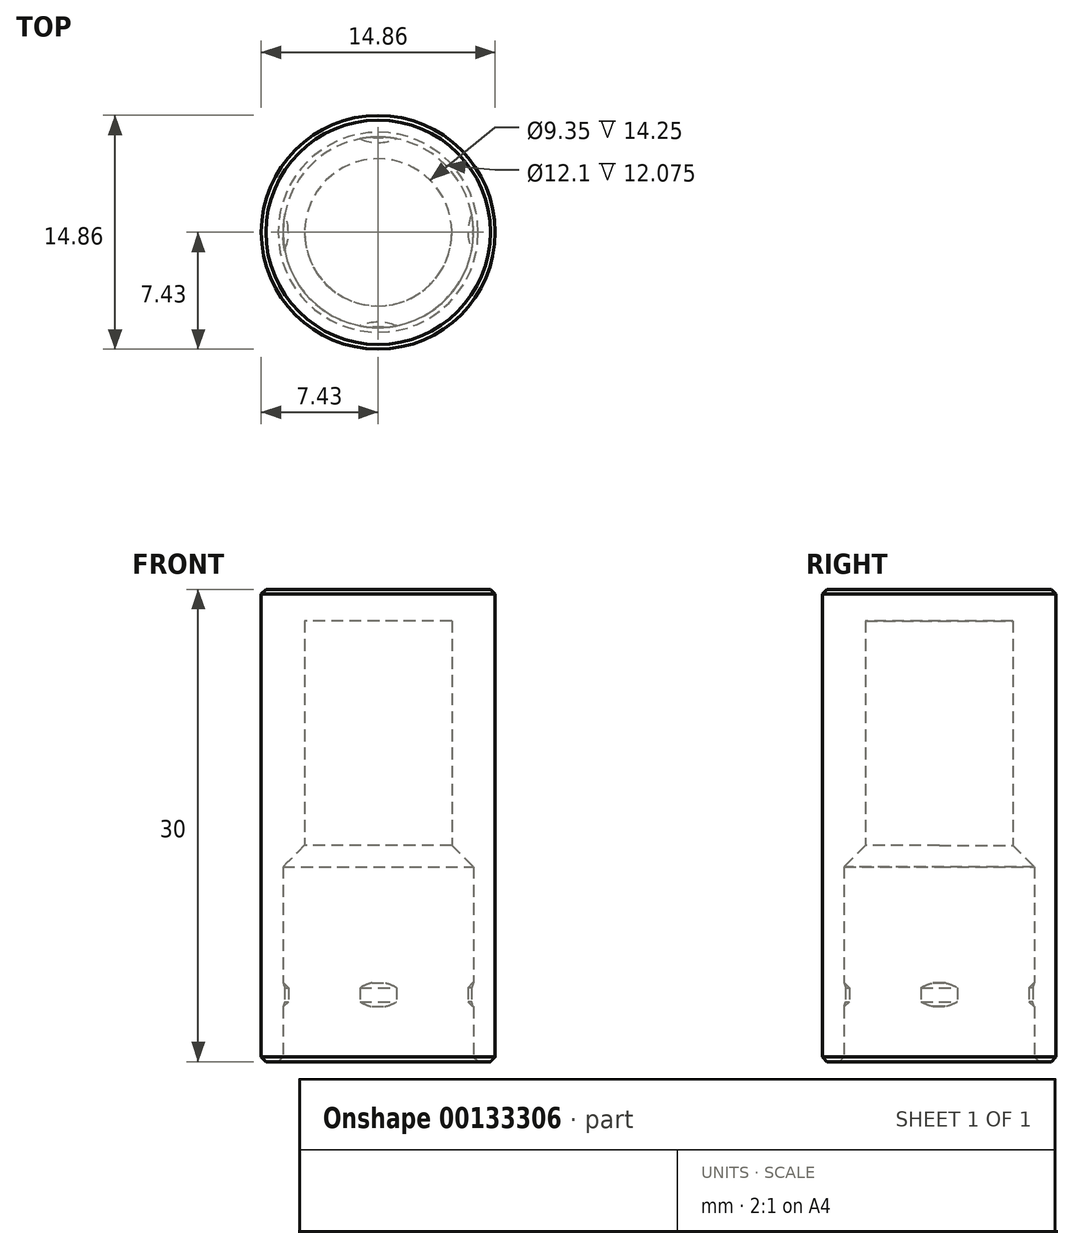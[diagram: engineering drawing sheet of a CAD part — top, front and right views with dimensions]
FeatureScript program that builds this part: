
annotation { "Feature Type Name" : "Feature", "Feature Type Description" : "" }
export const myFeature = defineFeature(function(context is Context, id is Id, definition is map)
    precondition{}
    {
        {
            assignVariable(context, id + "F0", {"name" : "ID", "anyValue" : 12});
        }
        {
            assignVariable(context, id + "F1", {"name" : "InsideCapID", "anyValue" : 9.25});
        }
        {
            var Q0;
            Q0=qCreatedBy(makeId("Top.planeOp"),FACE);
            var sketch = newSketch(context, id + "F2", { "sketchPlane" : qUnion([Q0])});
            skCircle(sketch, "E0", {"center": v(0, 0) * mm, "radius": 6.05 * mm});
            skArc(sketch, "E1", {"start": v(1.16, -5.94) * mm, "mid": v(0, -5.7) * mm, "end": v(-1.16, -5.94) * mm});
            skArc(sketch, "E2.1.0", {"start": v(5.94, 1.16) * mm, "mid": v(5.7, 0) * mm, "end": v(5.94, -1.16) * mm});
            skArc(sketch, "E2.2.0", {"start": v(-1.16, 5.94) * mm, "mid": v(0, 5.7) * mm, "end": v(1.16, 5.94) * mm});
            skArc(sketch, "E2.3.0", {"start": v(-5.94, -1.16) * mm, "mid": v(-5.7, 0) * mm, "end": v(-5.94, 1.16) * mm});
            skCircle(sketch, "E3.0", {"center": v(0, 0) * mm, "radius": 4.68 * mm});
            skCircle(sketch, "E4", {"center": v(0, 0) * mm, "radius": 7.42 * mm});
            skLineSegment(sketch, "E5", {"start": v(0, -4.68) * mm, "end": v(0, -6.05) * mm, "construction": true});
            skPoint(sketch, "E5.endSnap0", {"position": v(0, -5.36) * mm});
            skPoint(sketch, "E6", {"position": v(0, -5.7) * mm});
            skSolve(sketch);
        }
        {
            assignVariable(context, id + "F3", {"name" : "BumpStart", "anyValue" : 3.5});
        }
        {
            assignVariable(context, id + "F4", {"name" : "BumpEnd", "anyValue" : 5});
        }
        {
            assignVariable(context, id + "F5", {"name" : "InsideCapStart", "anyValue" : 11});
        }
        {
            assignVariable(context, id + "F6", {"name" : "Height", "anyValue" : 30});
        }
        {
            var Q0;
            Q0=makeQuery(id+"F2.imprint","IMPRINT",FACE,{"disambiguationData":[TD([[makeQuery(id+"F2.imprint","IMPRINT",EDGE,{"derivedFrom":sQuery(id+"F2.wireOp",EDGE,"E4")}),1.0]])]});
            extrude(context, id + "F7", {"entities" : qUnion([Q0]), "depth" : (getVariable(context, 'Height')) * mm});
        }
        {
            var Q0;
            {var subQ0=sQuery(id+"F2.wireOp",EDGE,"E2.3.0");Q0=makeQuery(id+"F2.imprint","IMPRINT",FACE,{"disambiguationData":[TD([[makeQuery(id+"F2.imprint","IMPRINT",EDGE,{"derivedFrom":subQ0}),1.0]])]});}
            var Q1;
            {var subQ0=sQuery(id+"F2.wireOp",EDGE,"E1");Q1=makeQuery(id+"F2.imprint","IMPRINT",FACE,{"disambiguationData":[TD([[makeQuery(id+"F2.imprint","IMPRINT",EDGE,{"derivedFrom":subQ0}),-1.0]])]});}
            var Q2;
            {var subQ0=sQuery(id+"F2.wireOp",EDGE,"E1");Q2=makeQuery(id+"F2.imprint","IMPRINT",FACE,{"disambiguationData":[TD([[makeQuery(id+"F2.imprint","IMPRINT",EDGE,{"derivedFrom":subQ0}),1.0]])]});}
            var Q3;
            {var subQ0=sQuery(id+"F2.wireOp",EDGE,"E2.1.0");Q3=makeQuery(id+"F2.imprint","IMPRINT",FACE,{"disambiguationData":[TD([[makeQuery(id+"F2.imprint","IMPRINT",EDGE,{"derivedFrom":subQ0}),1.0]])]});}
            var Q4;
            {var subQ0=sQuery(id+"F2.wireOp",EDGE,"E2.2.0");Q4=makeQuery(id+"F2.imprint","IMPRINT",FACE,{"disambiguationData":[TD([[makeQuery(id+"F2.imprint","IMPRINT",EDGE,{"derivedFrom":subQ0}),1.0]])]});}
            extrude(context, id + "F8", {"entities" : qUnion([Q0, Q1, Q2, Q3, Q4]), "operationType" : NewBodyOperationType.ADD, "depth" : (getVariable(context, 'Height')) * mm, "hasSecondDirection" : true, "secondDirectionOppositeDirection" : false, "secondDirectionDepth" : (getVariable(context, 'InsideCapStart')) * mm});
        }
        {
            var Q0;
            Q0=makeQuery(id+"F8.opExtrude","CAP_EDGE",EDGE,{"disambiguationData":[OSD([sQuery(id+"F2.wireOp",EDGE,"E3.0")])],"isStart":true});
            chamfer(context, id + "F9", {"entities" : qUnion([Q0]), "width" : (getVariable(context, 'ID') - getVariable(context, 'InsideCapID')) * mm, "tangentPropagation" : true});
        }
        {
            var Q0;
            {var subQ0=sQuery(id+"F2.wireOp",EDGE,"E2.3.0");Q0=makeQuery(id+"F2.imprint","IMPRINT",FACE,{"disambiguationData":[TD([[makeQuery(id+"F2.imprint","IMPRINT",EDGE,{"derivedFrom":subQ0}),1.0]])]});}
            var Q1;
            {var subQ0=sQuery(id+"F2.wireOp",EDGE,"E1");Q1=makeQuery(id+"F2.imprint","IMPRINT",FACE,{"disambiguationData":[TD([[makeQuery(id+"F2.imprint","IMPRINT",EDGE,{"derivedFrom":subQ0}),1.0]])]});}
            var Q2;
            {var subQ0=sQuery(id+"F2.wireOp",EDGE,"E2.1.0");Q2=makeQuery(id+"F2.imprint","IMPRINT",FACE,{"disambiguationData":[TD([[makeQuery(id+"F2.imprint","IMPRINT",EDGE,{"derivedFrom":subQ0}),1.0]])]});}
            var Q3;
            {var subQ0=sQuery(id+"F2.wireOp",EDGE,"E2.2.0");Q3=makeQuery(id+"F2.imprint","IMPRINT",FACE,{"disambiguationData":[TD([[makeQuery(id+"F2.imprint","IMPRINT",EDGE,{"derivedFrom":subQ0}),1.0]])]});}
            extrude(context, id + "F10", {"entities" : qUnion([Q0, Q1, Q2, Q3]), "operationType" : NewBodyOperationType.ADD, "depth" : (getVariable(context, 'BumpEnd')) * mm, "hasSecondDirection" : true, "secondDirectionOppositeDirection" : false, "secondDirectionDepth" : (getVariable(context, 'BumpStart')) * mm});
        }
        {
            var Q0;
            Q0=makeQuery(id+"F2.imprint","IMPRINT",FACE,{"disambiguationData":[TD([[makeQuery(id+"F2.imprint","IMPRINT",EDGE,{"derivedFrom":sQuery(id+"F2.wireOp",EDGE,"E3.0")}),1.0]])]});
            extrude(context, id + "F11", {"entities" : qUnion([Q0]), "operationType" : NewBodyOperationType.ADD, "depth" : (getVariable(context, 'Height')) * mm, "hasSecondDirection" : true, "secondDirectionOppositeDirection" : false, "secondDirectionDepth" : (getVariable(context, 'Height') - 2) * mm});
        }
        {
            var Q0;
            Q0=makeQuery(id+"F10.opExtrude","CAP_EDGE",EDGE,{"disambiguationData":[OSD([sQuery(id+"F2.wireOp",EDGE,"E2.3.0")])],"isStart":true});
            var Q1;
            Q1=makeQuery(id+"F10.opExtrude","CAP_EDGE",EDGE,{"disambiguationData":[OSD([sQuery(id+"F2.wireOp",EDGE,"E2.3.0")])],"isStart":false});
            var Q2;
            Q2=makeQuery(id+"F10.opExtrude","CAP_EDGE",EDGE,{"disambiguationData":[OSD([sQuery(id+"F2.wireOp",EDGE,"E1")])],"isStart":true});
            var Q3;
            Q3=makeQuery(id+"F10.opExtrude","CAP_EDGE",EDGE,{"disambiguationData":[OSD([sQuery(id+"F2.wireOp",EDGE,"E1")])],"isStart":false});
            var Q4;
            Q4=makeQuery(id+"F10.opExtrude","CAP_EDGE",EDGE,{"disambiguationData":[OSD([sQuery(id+"F2.wireOp",EDGE,"E2.2.0")])],"isStart":true});
            var Q5;
            Q5=makeQuery(id+"F10.opExtrude","CAP_EDGE",EDGE,{"disambiguationData":[OSD([sQuery(id+"F2.wireOp",EDGE,"E2.2.0")])],"isStart":false});
            var Q6;
            Q6=makeQuery(id+"F10.opExtrude","CAP_EDGE",EDGE,{"disambiguationData":[OSD([sQuery(id+"F2.wireOp",EDGE,"E2.1.0")])],"isStart":true});
            var Q7;
            Q7=makeQuery(id+"F10.opExtrude","CAP_EDGE",EDGE,{"disambiguationData":[OSD([sQuery(id+"F2.wireOp",EDGE,"E2.1.0")])],"isStart":false});
            chamfer(context, id + "F12", {"entities" : qUnion([Q0, Q1, Q2, Q3, Q4, Q5, Q6, Q7]), "width" : .3 * mm, "tangentPropagation" : true});
        }
        {
            var Q0;
            Q0=makeQuery(id+"F7.opExtrude","CAP_FACE",FACE,{"disambiguationData":[OSD([sQuery(id+"F2.wireOp",EDGE,"E0"),sQuery(id+"F2.wireOp",EDGE,"E4")])],"isStart":true});
            var Q1;
            {var subQ0=sQuery(id+"F2.wireOp",EDGE,"E3.0");var subQ1=sQuery(id+"F2.wireOp",EDGE,"E0");Q1=makeQuery(id+"F11.boolean.opBoolean","MERGE",FACE,{"derivedFrom":[makeQuery(id+"F8.boolean.opBoolean","MERGE",FACE,{"derivedFrom":[makeQuery(id+"F7.opExtrude","CAP_FACE",FACE,{"disambiguationData":[OSD([subQ1,sQuery(id+"F2.wireOp",EDGE,"E4")])],"isStart":false}),makeQuery(id+"F8.opExtrude","CAP_FACE",FACE,{"disambiguationData":[OSD([subQ1,subQ0])],"isStart":false})]}),makeQuery(id+"F11.opExtrude","CAP_FACE",FACE,{"disambiguationData":[OSD([subQ0])],"isStart":false})]});}
            chamfer(context, id + "F13", {"entities" : qUnion([Q0, Q1]), "width" : 0.3 * mm, "tangentPropagation" : true});
        }
    });
